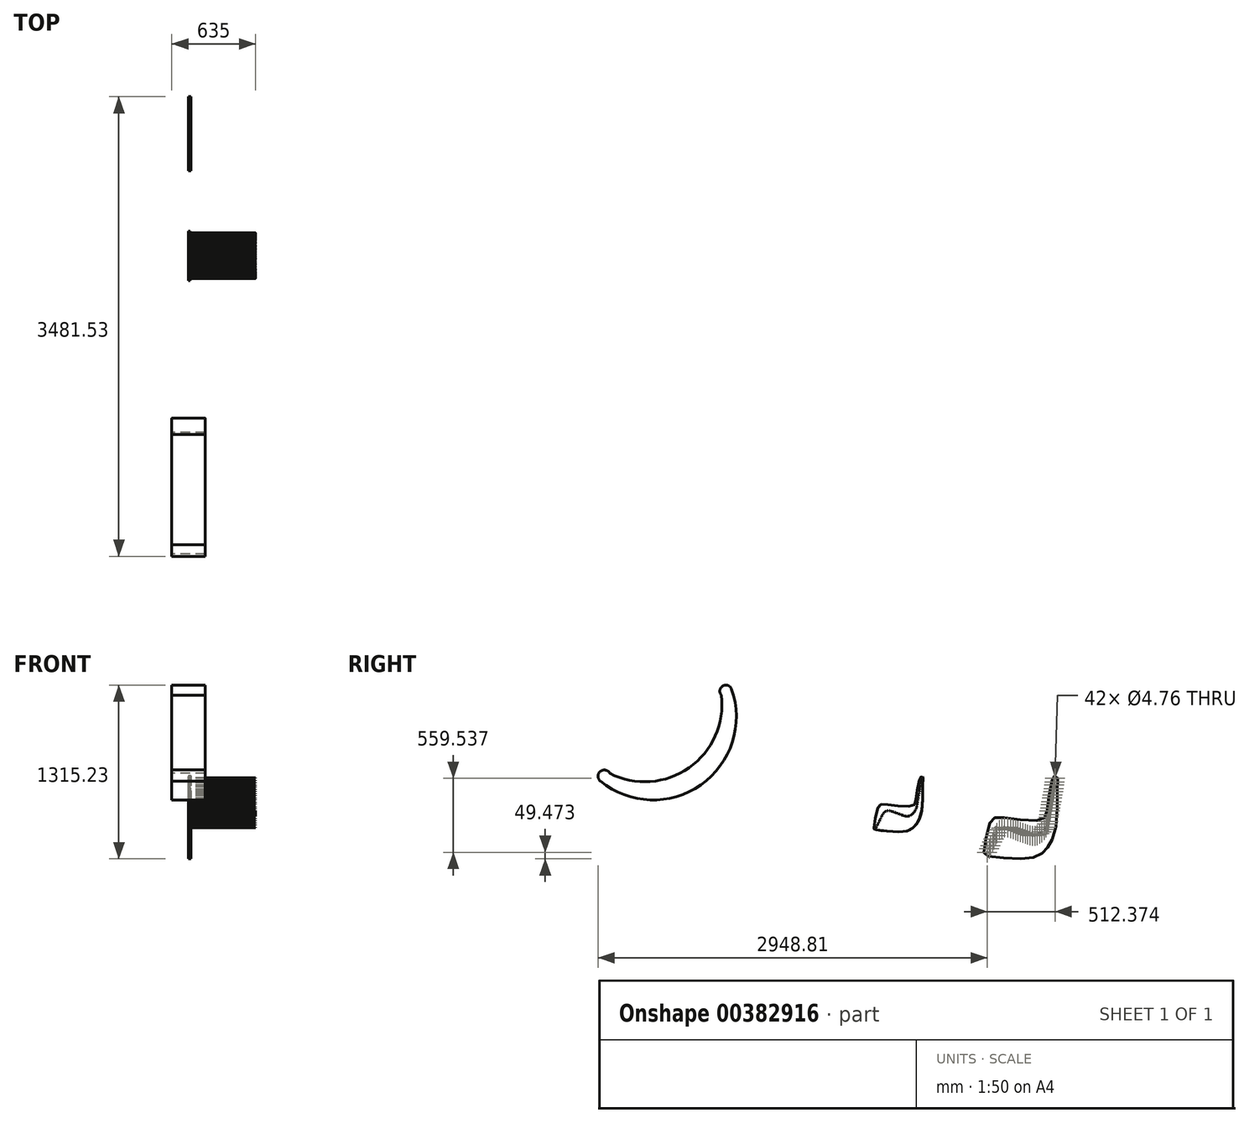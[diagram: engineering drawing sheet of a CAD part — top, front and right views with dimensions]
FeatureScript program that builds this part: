
annotation { "Feature Type Name" : "Feature", "Feature Type Description" : "" }
export const myFeature = defineFeature(function(context is Context, id is Id, definition is map)
    precondition{}
    {
        {
            var Q0;
            Q0=qCreatedBy(makeId("Right.planeOp"),FACE);
            var sketch = newSketch(context, id + "F0", { "sketchPlane" : qUnion([Q0])});
            skCircle(sketch, "E0", {"center": v(0, 0) * mm, "radius": 304.8 * mm});
            skLineSegment(sketch, "E1", {"start": v(-293.4, -82.59) * mm, "end": v(-78.09, -294.63) * mm});
            skCircle(sketch, "E2.0", {"center": v(0, 0) * mm, "radius": 381 * mm});
            skSolve(sketch);
        }
        {
            var Q0;
            Q0=qCreatedBy(makeId("Right.planeOp"),FACE);
            var sketch = newSketch(context, id + "F1", { "sketchPlane" : qUnion([Q0])});
            skArc(sketch, "E3", {"start": v(-480.61, -321.55) * mm, "mid": v(278.98, -347.7) * mm, "end": v(511.34, 375.95) * mm});
            skCircle(sketch, "E4", {"center": v(-452.9, -282.93) * mm, "radius": 47.53 * mm});
            skPoint(sketch, "E4.second.point", {"position": v(-410.62, -261.21) * mm});
            skPoint(sketch, "E4.third.point", {"position": v(-480.61, -244.32) * mm});
            skCircle(sketch, "E5", {"center": v(467.9, 361.15) * mm, "radius": 45.9 * mm});
            skPoint(sketch, "E5.second.point", {"position": v(434.1, 330.1) * mm});
            skPoint(sketch, "E5.third.point", {"position": v(424.45, 375.95) * mm});
            skArc(sketch, "E6", {"start": v(-410.62, -261.21) * mm, "mid": v(189.12, -218.95) * mm, "end": v(434.1, 330.1) * mm});
            skSolve(sketch);
        }
        {
            var Q0;
            Q0 = qSketchRegion(id + "F1", true);
            extrude(context, id + "F2", {"entities" : qUnion([Q0]), "endBound" : BoundingType.SYMMETRIC, "depth" : 254 * mm});
        }
        {
            var Q0;
            Q0=qCreatedBy(makeId("Right.planeOp"),FACE);
            var sketch = newSketch(context, id + "F3", { "sketchPlane" : qUnion([Q0])});
            skFitSpline(sketch, "E7", {"points": [v(1588.1, -672.39) * mm, v(1618.65, -522.75) * mm, v(1643, -495.6) * mm, v(1721.64, -500.28) * mm, v(1878.95, -507.77) * mm, v(1900.49, -487.17) * mm, v(1913.6, -410.39) * mm, v(1939.81, -289.6) * mm, v(1946.37, -285.85) * mm, v(1958.54, -285.79) * mm, v(1959.48, -320.5) * mm, v(1953.86, -522.75) * mm, v(1922.02, -627.62) * mm, v(1894.7, -664.12) * mm, v(1852.61, -693.43) * mm, v(1735.69, -702.53) * mm, v(1592.61, -684.79) * mm, v(1588.1, -672.39) * mm]});
            skFitSpline(sketch, "E8", {"points": [v(1839.42, 829.8) * mm, v(1806.64, 656.64) * mm, v(1782.3, 629.48) * mm, v(1703.64, 634.16) * mm, v(1546.34, 641.65) * mm, v(1524.8, 621.05) * mm, v(1511.7, 544.27) * mm, v(1485.47, 423.48) * mm, v(1478.92, 419.74) * mm, v(1466.75, 422.55) * mm, v(1465.81, 454.38) * mm, v(1471.43, 656.64) * mm, v(1503.27, 761.5) * mm, v(1546.34, 798.96) * mm, v(1596.9, 818.62) * mm, v(1689.6, 836.42) * mm, v(1834.27, 836.23) * mm, v(1839.42, 829.8) * mm]});
            skCircle(sketch, "E9", {"center": v(2585.3, 295.49) * mm, "radius": 304.8 * mm});
            skArc(sketch, "E10", {"start": v(2585.3, 295.49) * mm, "mid": v(2780.63, 386.57) * mm, "end": v(2689.55, 581.9) * mm});
            skArc(sketch, "E11", {"start": v(2585.3, 295.49) * mm, "mid": v(2389.96, 204.4) * mm, "end": v(2481.05, 9.07) * mm});
            skPoint(sketch, "E12.orphan", {"position": v(2689.55, 581.9) * mm});
            skCircle(sketch, "E13", {"center": v(2533.17, 152.28) * mm, "radius": 9.53 * mm});
            skCircle(sketch, "E14", {"center": v(2637.42, 438.7) * mm, "radius": 9.53 * mm});
            skFitSpline(sketch, "E15", {"points": [v(1606.22, -670.68) * mm, v(1621.17, -640.78) * mm, v(1637.56, -607.07) * mm, v(1653, -575.24) * mm, v(1675.01, -550.42) * mm, v(1702.63, -543.4) * mm, v(1730.26, -550.9) * mm, v(1756, -560.26) * mm, v(1780.82, -569.62) * mm, v(1805.16, -578.05) * mm, v(1829.98, -586) * mm, v(1856.2, -583.2) * mm, v(1879.14, -569.62) * mm, v(1899.74, -546.2) * mm, v(1913.31, -516.25) * mm, v(1918.93, -483.94) * mm, v(1924.55, -449.77) * mm, v(1930.64, -418.4) * mm, v(1935.63, -385.41) * mm, v(1941.76, -352) * mm, v(1945.93, -319.16) * mm, v(1949, -288.82) * mm], "startDerivative": vector(275.49, 563.46) * mm, "endDerivative": vector(62.5, 633.08) * mm});
            skCircle(sketch, "E16", {"center": v(1606.22, -670.68) * mm, "radius": 1.59 * mm});
            skCircle(sketch, "E17", {"center": v(1615.63, -651.8) * mm, "radius": 1.59 * mm});
            skCircle(sketch, "E18", {"center": v(1622.85, -637.43) * mm, "radius": 1.59 * mm});
            skCircle(sketch, "E19", {"center": v(1631.84, -619.24) * mm, "radius": 1.59 * mm});
            skCircle(sketch, "E20", {"center": v(1638.6, -604.78) * mm, "radius": 1.59 * mm});
            skCircle(sketch, "E21", {"center": v(1647.24, -586) * mm, "radius": 1.59 * mm});
            skCircle(sketch, "E22", {"center": v(1654.5, -572.78) * mm, "radius": 1.59 * mm});
            skCircle(sketch, "E23", {"center": v(1666.56, -557.28) * mm, "radius": 1.59 * mm});
            skCircle(sketch, "E24", {"center": v(1678.52, -548.4) * mm, "radius": 1.59 * mm});
            skCircle(sketch, "E25", {"center": v(1692.58, -543.84) * mm, "radius": 1.59 * mm});
            skCircle(sketch, "E26", {"center": v(1708.99, -544.23) * mm, "radius": 1.59 * mm});
            skCircle(sketch, "E27", {"center": v(1722.8, -548.17) * mm, "radius": 1.59 * mm});
            skCircle(sketch, "E28", {"center": v(1735.77, -552.9) * mm, "radius": 1.59 * mm});
            skCircle(sketch, "E29", {"center": v(1748.81, -557.6) * mm, "radius": 1.59 * mm});
            skCircle(sketch, "E30", {"center": v(1773.03, -566.76) * mm, "radius": 1.59 * mm});
            skCircle(sketch, "E31", {"center": v(1760.55, -561.98) * mm, "radius": 1.59 * mm});
            skCircle(sketch, "E32", {"center": v(1785.2, -571.14) * mm, "radius": 1.59 * mm});
            skCircle(sketch, "E33", {"center": v(1809.27, -579.63) * mm, "radius": 1.59 * mm});
            skCircle(sketch, "E34", {"center": v(1798.09, -575.5) * mm, "radius": 1.59 * mm});
            skCircle(sketch, "E35", {"center": v(1821.92, -584.19) * mm, "radius": 1.59 * mm});
            skCircle(sketch, "E36", {"center": v(1833.07, -586.35) * mm, "radius": 1.59 * mm});
            skCircle(sketch, "E37", {"center": v(1846.16, -585.75) * mm, "radius": 1.59 * mm});
            skCircle(sketch, "E38", {"center": v(1856.2, -583.2) * mm, "radius": 1.59 * mm});
            skCircle(sketch, "E39", {"center": v(1870, -576.41) * mm, "radius": 1.59 * mm});
            skCircle(sketch, "E40", {"center": v(1880.6, -568.35) * mm, "radius": 1.59 * mm});
            skCircle(sketch, "E41", {"center": v(1892.63, -555.8) * mm, "radius": 1.59 * mm});
            skCircle(sketch, "E42", {"center": v(1900.74, -544.22) * mm, "radius": 1.59 * mm});
            skCircle(sketch, "E43", {"center": v(1908.58, -528.02) * mm, "radius": 1.59 * mm});
            skCircle(sketch, "E44", {"center": v(1913.63, -514.07) * mm, "radius": 1.59 * mm});
            skCircle(sketch, "E45", {"center": v(1917.21, -494.8) * mm, "radius": 1.59 * mm});
            skCircle(sketch, "E46", {"center": v(1919.47, -480.2) * mm, "radius": 1.59 * mm});
            skCircle(sketch, "E47", {"center": v(1922.13, -461.07) * mm, "radius": 1.59 * mm});
            skCircle(sketch, "E48", {"center": v(1924.76, -447.99) * mm, "radius": 1.59 * mm});
            skCircle(sketch, "E49", {"center": v(1927.95, -429.8) * mm, "radius": 1.59 * mm});
            skCircle(sketch, "E50", {"center": v(1930.6, -415.05) * mm, "radius": 1.59 * mm});
            skCircle(sketch, "E51", {"center": v(1933.66, -396.85) * mm, "radius": 1.59 * mm});
            skCircle(sketch, "E52", {"center": v(1936.32, -381.97) * mm, "radius": 1.59 * mm});
            skCircle(sketch, "E53", {"center": v(1939.37, -364.04) * mm, "radius": 1.59 * mm});
            skCircle(sketch, "E54", {"center": v(1941.96, -349.47) * mm, "radius": 1.59 * mm});
            skCircle(sketch, "E55", {"center": v(1944.33, -330.83) * mm, "radius": 1.59 * mm});
            skCircle(sketch, "E56", {"center": v(1946.07, -316.14) * mm, "radius": 1.59 * mm});
            skCircle(sketch, "E57", {"center": v(1947.8, -297.66) * mm, "radius": 1.59 * mm});
            skLineSegment(sketch, "E58.bottom", {"start": v(2915.4, -134.35) * mm, "end": v(2331.2, -134.35) * mm});
            skLineSegment(sketch, "E58.top", {"start": v(2940.8, -743.95) * mm, "end": v(2331.2, -743.95) * mm});
            skLineSegment(sketch, "E58.left", {"start": v(2940.8, -134.35) * mm, "end": v(2940.8, -743.95) * mm});
            skLineSegment(sketch, "E58.right", {"start": v(2331.2, -134.35) * mm, "end": v(2331.2, -743.95) * mm});
            skLineSegment(sketch, "E59", {"start": v(2821.57, -439.15) * mm, "end": v(2455.55, -439.15) * mm});
            skLineSegment(sketch, "E60", {"start": v(2356.6, -743.95) * mm, "end": v(2331.2, -743.95) * mm});
            skLineSegment(sketch, "E61", {"start": v(2871.68, -396.7) * mm, "end": v(2915.4, -134.35) * mm});
            skLineSegment(sketch, "E62", {"start": v(2405.6, -480.66) * mm, "end": v(2356.6, -743.95) * mm});
            skPoint(sketch, "E63.visualSharp", {"position": v(2940.8, -134.35) * mm});
            skLineSegment(sketch, "E63.filletArc", {"start": v(2940.8, -134.35) * mm, "end": v(2940.8, -134.35) * mm});
            skPoint(sketch, "E64.visualSharp", {"position": v(2864.6, -439.15) * mm});
            skArc(sketch, "E64.filletArc", {"start": v(2821.57, -439.15) * mm, "mid": v(2854.4, -427.12) * mm, "end": v(2871.68, -396.7) * mm});
            skPoint(sketch, "E65.visualSharp", {"position": v(2413.33, -439.15) * mm});
            skArc(sketch, "E65.filletArc", {"start": v(2455.55, -439.15) * mm, "mid": v(2423.08, -450.89) * mm, "end": v(2405.6, -480.66) * mm});
            skPoint(sketch, "E66.visualSharp", {"position": v(2331.2, -134.35) * mm});
            skLineSegment(sketch, "E67.bottom", {"start": v(3735.99, -463.08) * mm, "end": v(3139.09, -463.08) * mm});
            skLineSegment(sketch, "E67.top", {"start": v(3735.99, -1072.68) * mm, "end": v(3126.39, -1072.68) * mm});
            skLineSegment(sketch, "E67.left", {"start": v(3735.99, -463.08) * mm, "end": v(3735.99, -1072.68) * mm});
            skLineSegment(sketch, "E67.right", {"start": v(3126.39, -475.78) * mm, "end": v(3126.39, -1072.68) * mm});
            skLineSegment(sketch, "E68", {"start": v(3611.45, -799.72) * mm, "end": v(3244.8, -799.72) * mm});
            skLineSegment(sketch, "E69", {"start": v(3151.79, -1072.68) * mm, "end": v(3126.39, -1072.68) * mm});
            skLineSegment(sketch, "E70", {"start": v(3661.56, -757.27) * mm, "end": v(3710.59, -463.08) * mm});
            skLineSegment(sketch, "E71", {"start": v(3194.86, -841.22) * mm, "end": v(3151.79, -1072.68) * mm});
            skPoint(sketch, "E72.visualSharp", {"position": v(3735.99, -463.08) * mm});
            skLineSegment(sketch, "E72.filletArc", {"start": v(3735.99, -463.08) * mm, "end": v(3735.99, -463.08) * mm});
            skPoint(sketch, "E73.visualSharp", {"position": v(3654.48, -799.72) * mm});
            skArc(sketch, "E73.filletArc", {"start": v(3611.45, -799.72) * mm, "mid": v(3644.28, -787.68) * mm, "end": v(3661.56, -757.27) * mm});
            skPoint(sketch, "E74.visualSharp", {"position": v(3202.59, -799.72) * mm});
            skArc(sketch, "E74.filletArc", {"start": v(3244.8, -799.72) * mm, "mid": v(3212.34, -811.45) * mm, "end": v(3194.86, -841.22) * mm});
            skPoint(sketch, "E75.visualSharp", {"position": v(3126.39, -463.08) * mm});
            skArc(sketch, "E75.filletArc", {"start": v(3139.09, -463.08) * mm, "mid": v(3130.1, -466.8) * mm, "end": v(3126.39, -475.78) * mm});
            skCircle(sketch, "E76", {"center": v(3722.26, -476.85) * mm, "radius": 13.77 * mm});
            skPoint(sketch, "E76.first.point", {"position": v(3735.99, -475.76) * mm});
            skPoint(sketch, "E76.second.point", {"position": v(3721.91, -463.08) * mm});
            skPoint(sketch, "E76.third.point", {"position": v(3708.69, -474.48) * mm});
            skLineSegment(sketch, "E77.bottom", {"start": v(3126.39, -1072.68) * mm, "end": v(3723.29, -1072.68) * mm});
            skLineSegment(sketch, "E77.top", {"start": v(3126.39, -463.08) * mm, "end": v(3735.99, -463.08) * mm});
            skLineSegment(sketch, "E77.left", {"start": v(3126.39, -1072.68) * mm, "end": v(3126.39, -463.08) * mm});
            skLineSegment(sketch, "E77.right", {"start": v(3735.99, -1059.98) * mm, "end": v(3735.99, -463.08) * mm});
            skLineSegment(sketch, "E78", {"start": v(3247.07, -759.21) * mm, "end": v(3613.26, -759.21) * mm});
            skLineSegment(sketch, "E79", {"start": v(3710.59, -463.08) * mm, "end": v(3735.99, -463.08) * mm});
            skLineSegment(sketch, "E80", {"start": v(3196.96, -801.66) * mm, "end": v(3151.79, -1072.68) * mm});
            skLineSegment(sketch, "E81", {"start": v(3663.2, -717.7) * mm, "end": v(3710.59, -463.08) * mm});
            skPoint(sketch, "E82.visualSharp", {"position": v(3126.39, -1072.68) * mm});
            skLineSegment(sketch, "E82.filletArc", {"start": v(4374.58, -603.6) * mm, "end": v(4374.58, -603.6) * mm});
            skPoint(sketch, "E83.visualSharp", {"position": v(3204.03, -759.21) * mm});
            skArc(sketch, "E83.filletArc", {"start": v(3247.07, -759.21) * mm, "mid": v(3214.23, -771.25) * mm, "end": v(3196.96, -801.66) * mm});
            skPoint(sketch, "E84.visualSharp", {"position": v(3655.47, -759.21) * mm});
            skArc(sketch, "E84.filletArc", {"start": v(3613.26, -759.21) * mm, "mid": v(3645.73, -747.48) * mm, "end": v(3663.2, -717.7) * mm});
            skPoint(sketch, "E85.visualSharp", {"position": v(3735.99, -1072.68) * mm});
            skArc(sketch, "E85.filletArc", {"start": v(3723.29, -1072.68) * mm, "mid": v(3732.27, -1068.96) * mm, "end": v(3735.99, -1059.98) * mm});
            skCircle(sketch, "E86", {"center": v(3140.12, -1058.91) * mm, "radius": 13.77 * mm});
            skPoint(sketch, "E86.first.point", {"position": v(3126.39, -1060) * mm});
            skPoint(sketch, "E86.second.point", {"position": v(3140.46, -1072.68) * mm});
            skPoint(sketch, "E86.third.point", {"position": v(3153.69, -1061.28) * mm});
            skFitSpline(sketch, "E87", {"points": [v(3126.39, -802.07) * mm, v(3137.63, -603.35) * mm, v(3162.08, -502.39) * mm, v(3219.46, -474.76) * mm, v(3365.05, -463.08) * mm, v(3593.52, -474.76) * mm, v(3690.22, -491.76) * mm, v(3700.6, -516.75) * mm], "startDerivative": vector(49.41, 1106.55) * mm, "endDerivative": vector(-78.89, -413.64) * mm});
            skLineSegment(sketch, "E88", {"start": v(2940.8, -134.35) * mm, "end": v(2915.4, -134.35) * mm});
            skFitSpline(sketch, "E89", {"points": [v(2331.2, -478.04) * mm, v(2342.68, -279.5) * mm, v(2367.12, -178.54) * mm, v(2424.5, -150.9) * mm, v(2570.1, -139.23) * mm, v(2798.57, -150.9) * mm, v(2895.27, -167.91) * mm, v(2905.65, -192.9) * mm], "startDerivative": vector(49.41, 1106.55) * mm, "endDerivative": vector(-68.57, -411.43) * mm});
            skCircle(sketch, "E90", {"center": v(2999.57, -107.75) * mm, "radius": 19.05 * mm});
            skFitSpline(sketch, "E91", {"points": [v(3299.06, -138.7) * mm, v(3304.9, -135.23) * mm, v(3310.44, -129.86) * mm, v(3312.49, -123.07) * mm, v(3309.8, -115.49) * mm, v(3304.12, -110.59) * mm, v(3297.32, -107.59) * mm, v(3290.37, -105.53) * mm, v(3283.9, -104.43) * mm, v(3276.63, -105.85) * mm, v(3269.84, -109.33) * mm, v(3266.68, -113.75) * mm, v(3268.42, -114.54) * mm, v(3272.05, -113.75) * mm, v(3278.37, -112.49) * mm, v(3281.69, -112.17) * mm, v(3283.27, -112.49) * mm, v(3279.63, -112.8) * mm, v(3273, -114.7) * mm, v(3266.52, -117.38) * mm, v(3260.83, -122.28) * mm, v(3256.41, -127.5) * mm, v(3253.1, -135.08) * mm, v(3256.25, -131.6) * mm, v(3257.1, -132.53) * mm, v(3259.1, -133.37) * mm, v(3262.68, -133.03) * mm, v(3269.29, -130.48) * mm, v(3277.66, -127.4) * mm, v(3287.77, -125.03) * mm, v(3295.35, -123.84) * mm, v(3300.8, -124.32) * mm, v(3303.01, -126.53) * mm, v(3303.64, -130.87) * mm, v(3302.07, -135.22) * mm, v(3298.8, -138.98) * mm, v(3298.8, -139) * mm], "startDerivative": vector(185.96, 100.47) * mm, "endDerivative": vector(3.82, -6.21) * mm});
            skFitSpline(sketch, "E92", {"points": [v(3287, -104.73) * mm, v(3284.28, -101.52) * mm, v(3275.78, -96.34) * mm, v(3258.25, -92.09) * mm, v(3234.87, -91.82) * mm, v(3213.88, -94.35) * mm, v(3191.56, -100.99) * mm, v(3174.7, -110.42) * mm, v(3167.26, -116.27) * mm], "startDerivative": vector(-33.94, 48.22) * mm, "endDerivative": vector(-67.07, -56.56) * mm});
            skFitSpline(sketch, "E93", {"points": [v(3167.26, -116.27) * mm, v(3178.56, -117.97) * mm, v(3187.4, -121.35) * mm], "startDerivative": vector(22.38, -2.25) * mm, "endDerivative": vector(17.81, -8.02) * mm});
            skLineSegment(sketch, "E94", {"start": v(3313.38, 1676.84) * mm, "end": v(3431.71, 1235.22) * mm});
            skLineSegment(sketch, "E95", {"start": v(3431.71, 1235.22) * mm, "end": v(3873.33, 1353.55) * mm});
            skLineSegment(sketch, "E96", {"start": v(3873.33, 1353.55) * mm, "end": v(3873.33, 1251.95) * mm});
            skLineSegment(sketch, "E97", {"start": v(3873.33, 1251.95) * mm, "end": v(3771.73, 1251.95) * mm});
            skLineSegment(sketch, "E98", {"start": v(3771.73, 1251.95) * mm, "end": v(3771.73, 1150.35) * mm});
            skLineSegment(sketch, "E99", {"start": v(3771.73, 1150.35) * mm, "end": v(3251.9, 1150.35) * mm});
            skLineSegment(sketch, "E100", {"start": v(3251.9, 1150.35) * mm, "end": v(3251.9, 1724.42) * mm});
            skLineSegment(sketch, "E101", {"start": v(3735.99, -761.53) * mm, "end": v(2999.92, -767.88) * mm, "construction": true});
            skPoint(sketch, "E101.endSnap0", {"position": v(3735.99, -767.88) * mm});
            skSolve(sketch);
        }
        {
            var Q0;
            Q0=makeQuery(id+"F3.imprint","IMPRINT",FACE,{"disambiguationData":[TD([[makeQuery(id+"F3.imprint","IMPRINT",EDGE,{"derivedFrom":sQuery(id+"F3.wireOp",EDGE,"E7")}),-1.0]])]});
            extrude(context, id + "F4", {"entities" : qUnion([Q0]), "depth" : 12.7 * mm});
        }
        {
            var Q0;
            Q0=makeQuery(id+"F4.opExtrude","SWEPT_BODY",BODY,{"disambiguationData":[OSD([sQuery(id+"F3.wireOp",EDGE,"E7")])]});
            var Q1;
            Q1=sQuery(id+"F0.wireOp",VERTEX,"E1.end");
            transform(context, id + "F5", {"entities" : qUnion([Q0]), "transformType" : TransformType.SCALE_UNIFORMLY, "scale" : 1.5, "scalePoint" : qUnion([Q1]), "makeCopy" : true});
        }
        {
            var Q0;
            {var subQ0=sQuery(id+"F3.wireOp",EDGE,"E35");var subQ1=sQuery(id+"F3.wireOp",EDGE,"E15");var subQ2=makeQuery(id+"F3.imprint","INTERSECT",VERTEX,{"disambiguationData":[OD(0.0)],"derivedFrom":[subQ1,subQ0]});Q0=makeQuery(id+"F3.imprint","IMPRINT",FACE,{"disambiguationData":[TD([[makeQuery(id+"F3.imprint","IMPRINT",EDGE,{"disambiguationData":[TD([[subQ2,-1.0]])],"derivedFrom":subQ1}),-1.0]])]});}
            var Q1;
            {var subQ0=sQuery(id+"F3.wireOp",EDGE,"E27");var subQ1=sQuery(id+"F3.wireOp",EDGE,"E15");var subQ2=makeQuery(id+"F3.imprint","INTERSECT",VERTEX,{"disambiguationData":[OD(0.0)],"derivedFrom":[subQ1,subQ0]});Q1=makeQuery(id+"F3.imprint","IMPRINT",FACE,{"disambiguationData":[TD([[makeQuery(id+"F3.imprint","IMPRINT",EDGE,{"disambiguationData":[TD([[subQ2,-1.0]])],"derivedFrom":subQ1}),-1.0]])]});}
            var Q2;
            {var subQ0=sQuery(id+"F3.wireOp",EDGE,"E39");var subQ1=sQuery(id+"F3.wireOp",EDGE,"E15");var subQ2=makeQuery(id+"F3.imprint","INTERSECT",VERTEX,{"disambiguationData":[OD(0.0)],"derivedFrom":[subQ1,subQ0]});Q2=makeQuery(id+"F3.imprint","IMPRINT",FACE,{"disambiguationData":[TD([[makeQuery(id+"F3.imprint","IMPRINT",EDGE,{"disambiguationData":[TD([[subQ2,-1.0]])],"derivedFrom":subQ1}),1.0]])]});}
            var Q3;
            {var subQ0=sQuery(id+"F3.wireOp",EDGE,"E32");var subQ1=sQuery(id+"F3.wireOp",EDGE,"E15");var subQ2=makeQuery(id+"F3.imprint","INTERSECT",VERTEX,{"disambiguationData":[OD(0.0)],"derivedFrom":[subQ1,subQ0]});Q3=makeQuery(id+"F3.imprint","IMPRINT",FACE,{"disambiguationData":[TD([[makeQuery(id+"F3.imprint","IMPRINT",EDGE,{"disambiguationData":[TD([[subQ2,-1.0]])],"derivedFrom":subQ1}),-1.0]])]});}
            var Q4;
            {var subQ0=sQuery(id+"F3.wireOp",EDGE,"E24");var subQ1=sQuery(id+"F3.wireOp",EDGE,"E15");var subQ2=makeQuery(id+"F3.imprint","INTERSECT",VERTEX,{"disambiguationData":[OD(0.0)],"derivedFrom":[subQ1,subQ0]});Q4=makeQuery(id+"F3.imprint","IMPRINT",FACE,{"disambiguationData":[TD([[makeQuery(id+"F3.imprint","IMPRINT",EDGE,{"disambiguationData":[TD([[subQ2,-1.0]])],"derivedFrom":subQ1}),1.0]])]});}
            var Q5;
            {var subQ0=sQuery(id+"F3.wireOp",EDGE,"E29");var subQ1=sQuery(id+"F3.wireOp",EDGE,"E15");var subQ2=makeQuery(id+"F3.imprint","INTERSECT",VERTEX,{"disambiguationData":[OD(0.0)],"derivedFrom":[subQ1,subQ0]});Q5=makeQuery(id+"F3.imprint","IMPRINT",FACE,{"disambiguationData":[TD([[makeQuery(id+"F3.imprint","IMPRINT",EDGE,{"disambiguationData":[TD([[subQ2,-1.0]])],"derivedFrom":subQ1}),-1.0]])]});}
            var Q6;
            {var subQ0=sQuery(id+"F3.wireOp",EDGE,"E42");var subQ1=sQuery(id+"F3.wireOp",EDGE,"E15");var subQ2=makeQuery(id+"F3.imprint","INTERSECT",VERTEX,{"disambiguationData":[OD(0.0)],"derivedFrom":[subQ1,subQ0]});Q6=makeQuery(id+"F3.imprint","IMPRINT",FACE,{"disambiguationData":[TD([[makeQuery(id+"F3.imprint","IMPRINT",EDGE,{"disambiguationData":[TD([[subQ2,-1.0]])],"derivedFrom":subQ1}),1.0]])]});}
            var Q7;
            {var subQ0=sQuery(id+"F3.wireOp",EDGE,"E33");var subQ1=sQuery(id+"F3.wireOp",EDGE,"E15");var subQ2=makeQuery(id+"F3.imprint","INTERSECT",VERTEX,{"disambiguationData":[OD(0.0)],"derivedFrom":[subQ1,subQ0]});Q7=makeQuery(id+"F3.imprint","IMPRINT",FACE,{"disambiguationData":[TD([[makeQuery(id+"F3.imprint","IMPRINT",EDGE,{"disambiguationData":[TD([[subQ2,-1.0]])],"derivedFrom":subQ1}),-1.0]])]});}
            var Q8;
            {var subQ0=sQuery(id+"F3.wireOp",EDGE,"E27");var subQ1=sQuery(id+"F3.wireOp",EDGE,"E15");var subQ2=makeQuery(id+"F3.imprint","INTERSECT",VERTEX,{"disambiguationData":[OD(0.0)],"derivedFrom":[subQ1,subQ0]});Q8=makeQuery(id+"F3.imprint","IMPRINT",FACE,{"disambiguationData":[TD([[makeQuery(id+"F3.imprint","IMPRINT",EDGE,{"disambiguationData":[TD([[subQ2,-1.0]])],"derivedFrom":subQ1}),1.0]])]});}
            var Q9;
            {var subQ0=sQuery(id+"F3.wireOp",EDGE,"E29");var subQ1=sQuery(id+"F3.wireOp",EDGE,"E15");var subQ2=makeQuery(id+"F3.imprint","INTERSECT",VERTEX,{"disambiguationData":[OD(0.0)],"derivedFrom":[subQ1,subQ0]});Q9=makeQuery(id+"F3.imprint","IMPRINT",FACE,{"disambiguationData":[TD([[makeQuery(id+"F3.imprint","IMPRINT",EDGE,{"disambiguationData":[TD([[subQ2,-1.0]])],"derivedFrom":subQ1}),1.0]])]});}
            var Q10;
            {var subQ0=sQuery(id+"F3.wireOp",EDGE,"E25");var subQ1=sQuery(id+"F3.wireOp",EDGE,"E15");var subQ2=makeQuery(id+"F3.imprint","INTERSECT",VERTEX,{"disambiguationData":[OD(0.0)],"derivedFrom":[subQ1,subQ0]});Q10=makeQuery(id+"F3.imprint","IMPRINT",FACE,{"disambiguationData":[TD([[makeQuery(id+"F3.imprint","IMPRINT",EDGE,{"disambiguationData":[TD([[subQ2,-1.0]])],"derivedFrom":subQ1}),1.0]])]});}
            var Q11;
            {var subQ0=sQuery(id+"F3.wireOp",EDGE,"E23");var subQ1=sQuery(id+"F3.wireOp",EDGE,"E15");var subQ2=makeQuery(id+"F3.imprint","INTERSECT",VERTEX,{"disambiguationData":[OD(0.0)],"derivedFrom":[subQ1,subQ0]});Q11=makeQuery(id+"F3.imprint","IMPRINT",FACE,{"disambiguationData":[TD([[makeQuery(id+"F3.imprint","IMPRINT",EDGE,{"disambiguationData":[TD([[subQ2,-1.0]])],"derivedFrom":subQ1}),1.0]])]});}
            var Q12;
            {var subQ0=sQuery(id+"F3.wireOp",EDGE,"E36");var subQ1=sQuery(id+"F3.wireOp",EDGE,"E15");var subQ2=makeQuery(id+"F3.imprint","INTERSECT",VERTEX,{"disambiguationData":[OD(0.0)],"derivedFrom":[subQ1,subQ0]});Q12=makeQuery(id+"F3.imprint","IMPRINT",FACE,{"disambiguationData":[TD([[makeQuery(id+"F3.imprint","IMPRINT",EDGE,{"disambiguationData":[TD([[subQ2,-1.0]])],"derivedFrom":subQ1}),1.0]])]});}
            var Q13;
            {var subQ0=sQuery(id+"F3.wireOp",EDGE,"E21");var subQ1=sQuery(id+"F3.wireOp",EDGE,"E15");var subQ2=makeQuery(id+"F3.imprint","INTERSECT",VERTEX,{"disambiguationData":[OD(0.0)],"derivedFrom":[subQ1,subQ0]});Q13=makeQuery(id+"F3.imprint","IMPRINT",FACE,{"disambiguationData":[TD([[makeQuery(id+"F3.imprint","IMPRINT",EDGE,{"disambiguationData":[TD([[subQ2,-1.0]])],"derivedFrom":subQ1}),1.0]])]});}
            var Q14;
            {var subQ0=sQuery(id+"F3.wireOp",EDGE,"E30");var subQ1=sQuery(id+"F3.wireOp",EDGE,"E15");var subQ2=makeQuery(id+"F3.imprint","INTERSECT",VERTEX,{"disambiguationData":[OD(0.0)],"derivedFrom":[subQ1,subQ0]});Q14=makeQuery(id+"F3.imprint","IMPRINT",FACE,{"disambiguationData":[TD([[makeQuery(id+"F3.imprint","IMPRINT",EDGE,{"disambiguationData":[TD([[subQ2,-1.0]])],"derivedFrom":subQ1}),-1.0]])]});}
            var Q15;
            {var subQ0=sQuery(id+"F3.wireOp",EDGE,"E33");var subQ1=sQuery(id+"F3.wireOp",EDGE,"E15");var subQ2=makeQuery(id+"F3.imprint","INTERSECT",VERTEX,{"disambiguationData":[OD(0.0)],"derivedFrom":[subQ1,subQ0]});Q15=makeQuery(id+"F3.imprint","IMPRINT",FACE,{"disambiguationData":[TD([[makeQuery(id+"F3.imprint","IMPRINT",EDGE,{"disambiguationData":[TD([[subQ2,-1.0]])],"derivedFrom":subQ1}),1.0]])]});}
            var Q16;
            {var subQ0=sQuery(id+"F3.wireOp",EDGE,"E31");var subQ1=sQuery(id+"F3.wireOp",EDGE,"E15");var subQ2=makeQuery(id+"F3.imprint","INTERSECT",VERTEX,{"disambiguationData":[OD(0.0)],"derivedFrom":[subQ1,subQ0]});Q16=makeQuery(id+"F3.imprint","IMPRINT",FACE,{"disambiguationData":[TD([[makeQuery(id+"F3.imprint","IMPRINT",EDGE,{"disambiguationData":[TD([[subQ2,-1.0]])],"derivedFrom":subQ1}),1.0]])]});}
            var Q17;
            {var subQ0=sQuery(id+"F3.wireOp",EDGE,"E23");var subQ1=sQuery(id+"F3.wireOp",EDGE,"E15");var subQ2=makeQuery(id+"F3.imprint","INTERSECT",VERTEX,{"disambiguationData":[OD(0.0)],"derivedFrom":[subQ1,subQ0]});Q17=makeQuery(id+"F3.imprint","IMPRINT",FACE,{"disambiguationData":[TD([[makeQuery(id+"F3.imprint","IMPRINT",EDGE,{"disambiguationData":[TD([[subQ2,-1.0]])],"derivedFrom":subQ1}),-1.0]])]});}
            var Q18;
            {var subQ0=sQuery(id+"F3.wireOp",EDGE,"E28");var subQ1=sQuery(id+"F3.wireOp",EDGE,"E15");var subQ2=makeQuery(id+"F3.imprint","INTERSECT",VERTEX,{"disambiguationData":[OD(0.0)],"derivedFrom":[subQ1,subQ0]});Q18=makeQuery(id+"F3.imprint","IMPRINT",FACE,{"disambiguationData":[TD([[makeQuery(id+"F3.imprint","IMPRINT",EDGE,{"disambiguationData":[TD([[subQ2,-1.0]])],"derivedFrom":subQ1}),-1.0]])]});}
            var Q19;
            {var subQ0=sQuery(id+"F3.wireOp",EDGE,"E26");var subQ1=sQuery(id+"F3.wireOp",EDGE,"E15");var subQ2=makeQuery(id+"F3.imprint","INTERSECT",VERTEX,{"disambiguationData":[OD(0.0)],"derivedFrom":[subQ1,subQ0]});Q19=makeQuery(id+"F3.imprint","IMPRINT",FACE,{"disambiguationData":[TD([[makeQuery(id+"F3.imprint","IMPRINT",EDGE,{"disambiguationData":[TD([[subQ2,-1.0]])],"derivedFrom":subQ1}),1.0]])]});}
            var Q20;
            {var subQ0=sQuery(id+"F3.wireOp",EDGE,"E36");var subQ1=sQuery(id+"F3.wireOp",EDGE,"E15");var subQ2=makeQuery(id+"F3.imprint","INTERSECT",VERTEX,{"disambiguationData":[OD(0.0)],"derivedFrom":[subQ1,subQ0]});Q20=makeQuery(id+"F3.imprint","IMPRINT",FACE,{"disambiguationData":[TD([[makeQuery(id+"F3.imprint","IMPRINT",EDGE,{"disambiguationData":[TD([[subQ2,-1.0]])],"derivedFrom":subQ1}),-1.0]])]});}
            var Q21;
            {var subQ0=sQuery(id+"F3.wireOp",EDGE,"E37");var subQ1=sQuery(id+"F3.wireOp",EDGE,"E15");var subQ2=makeQuery(id+"F3.imprint","INTERSECT",VERTEX,{"disambiguationData":[OD(0.0)],"derivedFrom":[subQ1,subQ0]});Q21=makeQuery(id+"F3.imprint","IMPRINT",FACE,{"disambiguationData":[TD([[makeQuery(id+"F3.imprint","IMPRINT",EDGE,{"disambiguationData":[TD([[subQ2,-1.0]])],"derivedFrom":subQ1}),1.0]])]});}
            var Q22;
            {var subQ0=sQuery(id+"F3.wireOp",EDGE,"E41");var subQ1=sQuery(id+"F3.wireOp",EDGE,"E15");var subQ2=makeQuery(id+"F3.imprint","INTERSECT",VERTEX,{"disambiguationData":[OD(0.0)],"derivedFrom":[subQ1,subQ0]});Q22=makeQuery(id+"F3.imprint","IMPRINT",FACE,{"disambiguationData":[TD([[makeQuery(id+"F3.imprint","IMPRINT",EDGE,{"disambiguationData":[TD([[subQ2,-1.0]])],"derivedFrom":subQ1}),-1.0]])]});}
            var Q23;
            {var subQ0=sQuery(id+"F3.wireOp",EDGE,"E34");var subQ1=sQuery(id+"F3.wireOp",EDGE,"E15");var subQ2=makeQuery(id+"F3.imprint","INTERSECT",VERTEX,{"disambiguationData":[OD(0.0)],"derivedFrom":[subQ1,subQ0]});Q23=makeQuery(id+"F3.imprint","IMPRINT",FACE,{"disambiguationData":[TD([[makeQuery(id+"F3.imprint","IMPRINT",EDGE,{"disambiguationData":[TD([[subQ2,-1.0]])],"derivedFrom":subQ1}),1.0]])]});}
            var Q24;
            {var subQ0=sQuery(id+"F3.wireOp",EDGE,"E37");var subQ1=sQuery(id+"F3.wireOp",EDGE,"E15");var subQ2=makeQuery(id+"F3.imprint","INTERSECT",VERTEX,{"disambiguationData":[OD(0.0)],"derivedFrom":[subQ1,subQ0]});Q24=makeQuery(id+"F3.imprint","IMPRINT",FACE,{"disambiguationData":[TD([[makeQuery(id+"F3.imprint","IMPRINT",EDGE,{"disambiguationData":[TD([[subQ2,-1.0]])],"derivedFrom":subQ1}),-1.0]])]});}
            var Q25;
            {var subQ0=sQuery(id+"F3.wireOp",EDGE,"E30");var subQ1=sQuery(id+"F3.wireOp",EDGE,"E15");var subQ2=makeQuery(id+"F3.imprint","INTERSECT",VERTEX,{"disambiguationData":[OD(0.0)],"derivedFrom":[subQ1,subQ0]});Q25=makeQuery(id+"F3.imprint","IMPRINT",FACE,{"disambiguationData":[TD([[makeQuery(id+"F3.imprint","IMPRINT",EDGE,{"disambiguationData":[TD([[subQ2,-1.0]])],"derivedFrom":subQ1}),1.0]])]});}
            var Q26;
            {var subQ0=sQuery(id+"F3.wireOp",EDGE,"E40");var subQ1=sQuery(id+"F3.wireOp",EDGE,"E15");var subQ2=makeQuery(id+"F3.imprint","INTERSECT",VERTEX,{"disambiguationData":[OD(0.0)],"derivedFrom":[subQ1,subQ0]});Q26=makeQuery(id+"F3.imprint","IMPRINT",FACE,{"disambiguationData":[TD([[makeQuery(id+"F3.imprint","IMPRINT",EDGE,{"disambiguationData":[TD([[subQ2,-1.0]])],"derivedFrom":subQ1}),1.0]])]});}
            var Q27;
            {var subQ0=sQuery(id+"F3.wireOp",EDGE,"E21");var subQ1=sQuery(id+"F3.wireOp",EDGE,"E15");var subQ2=makeQuery(id+"F3.imprint","INTERSECT",VERTEX,{"disambiguationData":[OD(0.0)],"derivedFrom":[subQ1,subQ0]});Q27=makeQuery(id+"F3.imprint","IMPRINT",FACE,{"disambiguationData":[TD([[makeQuery(id+"F3.imprint","IMPRINT",EDGE,{"disambiguationData":[TD([[subQ2,-1.0]])],"derivedFrom":subQ1}),-1.0]])]});}
            var Q28;
            {var subQ0=sQuery(id+"F3.wireOp",EDGE,"E34");var subQ1=sQuery(id+"F3.wireOp",EDGE,"E15");var subQ2=makeQuery(id+"F3.imprint","INTERSECT",VERTEX,{"disambiguationData":[OD(0.0)],"derivedFrom":[subQ1,subQ0]});Q28=makeQuery(id+"F3.imprint","IMPRINT",FACE,{"disambiguationData":[TD([[makeQuery(id+"F3.imprint","IMPRINT",EDGE,{"disambiguationData":[TD([[subQ2,-1.0]])],"derivedFrom":subQ1}),-1.0]])]});}
            var Q29;
            {var subQ0=sQuery(id+"F3.wireOp",EDGE,"E26");var subQ1=sQuery(id+"F3.wireOp",EDGE,"E15");var subQ2=makeQuery(id+"F3.imprint","INTERSECT",VERTEX,{"disambiguationData":[OD(0.0)],"derivedFrom":[subQ1,subQ0]});Q29=makeQuery(id+"F3.imprint","IMPRINT",FACE,{"disambiguationData":[TD([[makeQuery(id+"F3.imprint","IMPRINT",EDGE,{"disambiguationData":[TD([[subQ2,-1.0]])],"derivedFrom":subQ1}),-1.0]])]});}
            var Q30;
            {var subQ0=sQuery(id+"F3.wireOp",EDGE,"E31");var subQ1=sQuery(id+"F3.wireOp",EDGE,"E15");var subQ2=makeQuery(id+"F3.imprint","INTERSECT",VERTEX,{"disambiguationData":[OD(0.0)],"derivedFrom":[subQ1,subQ0]});Q30=makeQuery(id+"F3.imprint","IMPRINT",FACE,{"disambiguationData":[TD([[makeQuery(id+"F3.imprint","IMPRINT",EDGE,{"disambiguationData":[TD([[subQ2,-1.0]])],"derivedFrom":subQ1}),-1.0]])]});}
            var Q31;
            {var subQ0=sQuery(id+"F3.wireOp",EDGE,"E22");var subQ1=sQuery(id+"F3.wireOp",EDGE,"E15");var subQ2=makeQuery(id+"F3.imprint","INTERSECT",VERTEX,{"disambiguationData":[OD(0.0)],"derivedFrom":[subQ1,subQ0]});Q31=makeQuery(id+"F3.imprint","IMPRINT",FACE,{"disambiguationData":[TD([[makeQuery(id+"F3.imprint","IMPRINT",EDGE,{"disambiguationData":[TD([[subQ2,-1.0]])],"derivedFrom":subQ1}),1.0]])]});}
            var Q32;
            {var subQ0=sQuery(id+"F3.wireOp",EDGE,"E25");var subQ1=sQuery(id+"F3.wireOp",EDGE,"E15");var subQ2=makeQuery(id+"F3.imprint","INTERSECT",VERTEX,{"disambiguationData":[OD(0.0)],"derivedFrom":[subQ1,subQ0]});Q32=makeQuery(id+"F3.imprint","IMPRINT",FACE,{"disambiguationData":[TD([[makeQuery(id+"F3.imprint","IMPRINT",EDGE,{"disambiguationData":[TD([[subQ2,-1.0]])],"derivedFrom":subQ1}),-1.0]])]});}
            var Q33;
            {var subQ0=sQuery(id+"F3.wireOp",EDGE,"E28");var subQ1=sQuery(id+"F3.wireOp",EDGE,"E15");var subQ2=makeQuery(id+"F3.imprint","INTERSECT",VERTEX,{"disambiguationData":[OD(0.0)],"derivedFrom":[subQ1,subQ0]});Q33=makeQuery(id+"F3.imprint","IMPRINT",FACE,{"disambiguationData":[TD([[makeQuery(id+"F3.imprint","IMPRINT",EDGE,{"disambiguationData":[TD([[subQ2,-1.0]])],"derivedFrom":subQ1}),1.0]])]});}
            var Q34;
            {var subQ0=sQuery(id+"F3.wireOp",EDGE,"E35");var subQ1=sQuery(id+"F3.wireOp",EDGE,"E15");var subQ2=makeQuery(id+"F3.imprint","INTERSECT",VERTEX,{"disambiguationData":[OD(0.0)],"derivedFrom":[subQ1,subQ0]});Q34=makeQuery(id+"F3.imprint","IMPRINT",FACE,{"disambiguationData":[TD([[makeQuery(id+"F3.imprint","IMPRINT",EDGE,{"disambiguationData":[TD([[subQ2,-1.0]])],"derivedFrom":subQ1}),1.0]])]});}
            var Q35;
            {var subQ0=sQuery(id+"F3.wireOp",EDGE,"E24");var subQ1=sQuery(id+"F3.wireOp",EDGE,"E15");var subQ2=makeQuery(id+"F3.imprint","INTERSECT",VERTEX,{"disambiguationData":[OD(0.0)],"derivedFrom":[subQ1,subQ0]});Q35=makeQuery(id+"F3.imprint","IMPRINT",FACE,{"disambiguationData":[TD([[makeQuery(id+"F3.imprint","IMPRINT",EDGE,{"disambiguationData":[TD([[subQ2,-1.0]])],"derivedFrom":subQ1}),-1.0]])]});}
            var Q36;
            {var subQ0=sQuery(id+"F3.wireOp",EDGE,"E41");var subQ1=sQuery(id+"F3.wireOp",EDGE,"E15");var subQ2=makeQuery(id+"F3.imprint","INTERSECT",VERTEX,{"disambiguationData":[OD(0.0)],"derivedFrom":[subQ1,subQ0]});Q36=makeQuery(id+"F3.imprint","IMPRINT",FACE,{"disambiguationData":[TD([[makeQuery(id+"F3.imprint","IMPRINT",EDGE,{"disambiguationData":[TD([[subQ2,-1.0]])],"derivedFrom":subQ1}),1.0]])]});}
            var Q37;
            {var subQ0=sQuery(id+"F3.wireOp",EDGE,"E42");var subQ1=sQuery(id+"F3.wireOp",EDGE,"E15");var subQ2=makeQuery(id+"F3.imprint","INTERSECT",VERTEX,{"disambiguationData":[OD(0.0)],"derivedFrom":[subQ1,subQ0]});Q37=makeQuery(id+"F3.imprint","IMPRINT",FACE,{"disambiguationData":[TD([[makeQuery(id+"F3.imprint","IMPRINT",EDGE,{"disambiguationData":[TD([[subQ2,-1.0]])],"derivedFrom":subQ1}),-1.0]])]});}
            var Q38;
            {var subQ0=sQuery(id+"F3.wireOp",EDGE,"E40");var subQ1=sQuery(id+"F3.wireOp",EDGE,"E15");var subQ2=makeQuery(id+"F3.imprint","INTERSECT",VERTEX,{"disambiguationData":[OD(0.0)],"derivedFrom":[subQ1,subQ0]});Q38=makeQuery(id+"F3.imprint","IMPRINT",FACE,{"disambiguationData":[TD([[makeQuery(id+"F3.imprint","IMPRINT",EDGE,{"disambiguationData":[TD([[subQ2,-1.0]])],"derivedFrom":subQ1}),-1.0]])]});}
            var Q39;
            {var subQ0=sQuery(id+"F3.wireOp",EDGE,"9f402305-efcd-4aa8-bc8a-3394f6d3dfb0");var subQ1=sQuery(id+"F3.wireOp",EDGE,"E15");var subQ2=makeQuery(id+"F3.imprint","INTERSECT",VERTEX,{"disambiguationData":[OD(0.0)],"derivedFrom":[subQ1,subQ0]});Q39=makeQuery(id+"F3.imprint","IMPRINT",FACE,{"disambiguationData":[TD([[makeQuery(id+"F3.imprint","IMPRINT",EDGE,{"disambiguationData":[TD([[subQ2,-1.0]])],"derivedFrom":subQ1}),1.0]])]});}
            var Q40;
            {var subQ0=sQuery(id+"F3.wireOp",EDGE,"E39");var subQ1=sQuery(id+"F3.wireOp",EDGE,"E15");var subQ2=makeQuery(id+"F3.imprint","INTERSECT",VERTEX,{"disambiguationData":[OD(0.0)],"derivedFrom":[subQ1,subQ0]});Q40=makeQuery(id+"F3.imprint","IMPRINT",FACE,{"disambiguationData":[TD([[makeQuery(id+"F3.imprint","IMPRINT",EDGE,{"disambiguationData":[TD([[subQ2,-1.0]])],"derivedFrom":subQ1}),-1.0]])]});}
            var Q41;
            {var subQ0=sQuery(id+"F3.wireOp",EDGE,"E22");var subQ1=sQuery(id+"F3.wireOp",EDGE,"E15");var subQ2=makeQuery(id+"F3.imprint","INTERSECT",VERTEX,{"disambiguationData":[OD(0.0)],"derivedFrom":[subQ1,subQ0]});Q41=makeQuery(id+"F3.imprint","IMPRINT",FACE,{"disambiguationData":[TD([[makeQuery(id+"F3.imprint","IMPRINT",EDGE,{"disambiguationData":[TD([[subQ2,-1.0]])],"derivedFrom":subQ1}),-1.0]])]});}
            var Q42;
            {var subQ0=sQuery(id+"F3.wireOp",EDGE,"E32");var subQ1=sQuery(id+"F3.wireOp",EDGE,"E15");var subQ2=makeQuery(id+"F3.imprint","INTERSECT",VERTEX,{"disambiguationData":[OD(0.0)],"derivedFrom":[subQ1,subQ0]});Q42=makeQuery(id+"F3.imprint","IMPRINT",FACE,{"disambiguationData":[TD([[makeQuery(id+"F3.imprint","IMPRINT",EDGE,{"disambiguationData":[TD([[subQ2,-1.0]])],"derivedFrom":subQ1}),1.0]])]});}
            var Q43;
            {var subQ0=sQuery(id+"F3.wireOp",EDGE,"9f402305-efcd-4aa8-bc8a-3394f6d3dfb0");var subQ1=sQuery(id+"F3.wireOp",EDGE,"E15");var subQ2=makeQuery(id+"F3.imprint","INTERSECT",VERTEX,{"disambiguationData":[OD(0.0)],"derivedFrom":[subQ1,subQ0]});Q43=makeQuery(id+"F3.imprint","IMPRINT",FACE,{"disambiguationData":[TD([[makeQuery(id+"F3.imprint","IMPRINT",EDGE,{"disambiguationData":[TD([[subQ2,-1.0]])],"derivedFrom":subQ1}),-1.0]])]});}
            var Q44;
            {var subQ0=sQuery(id+"F3.wireOp",EDGE,"E38");var subQ1=sQuery(id+"F3.wireOp",EDGE,"E15");var subQ2=makeQuery(id+"F3.imprint","INTERSECT",VERTEX,{"disambiguationData":[OD(0.0)],"derivedFrom":[subQ1,subQ0]});Q44=makeQuery(id+"F3.imprint","IMPRINT",FACE,{"disambiguationData":[TD([[makeQuery(id+"F3.imprint","IMPRINT",EDGE,{"disambiguationData":[TD([[subQ2,-1.0]])],"derivedFrom":subQ1}),1.0]])]});}
            var Q45;
            {var subQ0=sQuery(id+"F3.wireOp",EDGE,"E38");var subQ1=sQuery(id+"F3.wireOp",EDGE,"E15");var subQ2=makeQuery(id+"F3.imprint","INTERSECT",VERTEX,{"disambiguationData":[OD(0.0)],"derivedFrom":[subQ1,subQ0]});Q45=makeQuery(id+"F3.imprint","IMPRINT",FACE,{"disambiguationData":[TD([[makeQuery(id+"F3.imprint","IMPRINT",EDGE,{"disambiguationData":[TD([[subQ2,-1.0]])],"derivedFrom":subQ1}),-1.0]])]});}
            var Q46;
            {var subQ0=sQuery(id+"F3.wireOp",EDGE,"E39");var subQ1=sQuery(id+"F3.wireOp",EDGE,"E15");var subQ2=makeQuery(id+"F3.imprint","INTERSECT",VERTEX,{"disambiguationData":[OD(1.0)],"derivedFrom":[subQ1,subQ0]});Q46=makeQuery(id+"F3.imprint","IMPRINT",FACE,{"disambiguationData":[TD([[makeQuery(id+"F3.imprint","IMPRINT",EDGE,{"disambiguationData":[TD([[subQ2,1.0]])],"derivedFrom":subQ1}),-1.0]])]});}
            var Q47;
            {var subQ0=sQuery(id+"F3.wireOp",EDGE,"E19");var subQ1=sQuery(id+"F3.wireOp",EDGE,"E15");var subQ2=makeQuery(id+"F3.imprint","INTERSECT",VERTEX,{"disambiguationData":[OD(0.0)],"derivedFrom":[subQ1,subQ0]});Q47=makeQuery(id+"F3.imprint","IMPRINT",FACE,{"disambiguationData":[TD([[makeQuery(id+"F3.imprint","IMPRINT",EDGE,{"disambiguationData":[TD([[subQ2,-1.0]])],"derivedFrom":subQ1}),-1.0]])]});}
            var Q48;
            {var subQ0=sQuery(id+"F3.wireOp",EDGE,"E18");var subQ1=sQuery(id+"F3.wireOp",EDGE,"E15");var subQ2=makeQuery(id+"F3.imprint","INTERSECT",VERTEX,{"disambiguationData":[OD(0.0)],"derivedFrom":[subQ1,subQ0]});Q48=makeQuery(id+"F3.imprint","IMPRINT",FACE,{"disambiguationData":[TD([[makeQuery(id+"F3.imprint","IMPRINT",EDGE,{"disambiguationData":[TD([[subQ2,-1.0]])],"derivedFrom":subQ1}),1.0]])]});}
            var Q49;
            {var subQ0=sQuery(id+"F3.wireOp",EDGE,"E17");var subQ1=sQuery(id+"F3.wireOp",EDGE,"E15");var subQ2=makeQuery(id+"F3.imprint","INTERSECT",VERTEX,{"disambiguationData":[OD(0.0)],"derivedFrom":[subQ1,subQ0]});Q49=makeQuery(id+"F3.imprint","IMPRINT",FACE,{"disambiguationData":[TD([[makeQuery(id+"F3.imprint","IMPRINT",EDGE,{"disambiguationData":[TD([[subQ2,-1.0]])],"derivedFrom":subQ1}),1.0]])]});}
            var Q50;
            {var subQ0=sQuery(id+"F3.wireOp",EDGE,"E19");var subQ1=sQuery(id+"F3.wireOp",EDGE,"E15");var subQ2=makeQuery(id+"F3.imprint","INTERSECT",VERTEX,{"disambiguationData":[OD(0.0)],"derivedFrom":[subQ1,subQ0]});Q50=makeQuery(id+"F3.imprint","IMPRINT",FACE,{"disambiguationData":[TD([[makeQuery(id+"F3.imprint","IMPRINT",EDGE,{"disambiguationData":[TD([[subQ2,-1.0]])],"derivedFrom":subQ1}),1.0]])]});}
            var Q51;
            {var subQ0=sQuery(id+"F3.wireOp",EDGE,"E18");var subQ1=sQuery(id+"F3.wireOp",EDGE,"E15");var subQ2=makeQuery(id+"F3.imprint","INTERSECT",VERTEX,{"disambiguationData":[OD(0.0)],"derivedFrom":[subQ1,subQ0]});Q51=makeQuery(id+"F3.imprint","IMPRINT",FACE,{"disambiguationData":[TD([[makeQuery(id+"F3.imprint","IMPRINT",EDGE,{"disambiguationData":[TD([[subQ2,-1.0]])],"derivedFrom":subQ1}),-1.0]])]});}
            var Q52;
            {var subQ0=sQuery(id+"F3.wireOp",EDGE,"E20");var subQ1=sQuery(id+"F3.wireOp",EDGE,"E15");var subQ2=makeQuery(id+"F3.imprint","INTERSECT",VERTEX,{"disambiguationData":[OD(0.0)],"derivedFrom":[subQ1,subQ0]});Q52=makeQuery(id+"F3.imprint","IMPRINT",FACE,{"disambiguationData":[TD([[makeQuery(id+"F3.imprint","IMPRINT",EDGE,{"disambiguationData":[TD([[subQ2,-1.0]])],"derivedFrom":subQ1}),1.0]])]});}
            var Q53;
            {var subQ0=sQuery(id+"F3.wireOp",EDGE,"E17");var subQ1=sQuery(id+"F3.wireOp",EDGE,"E15");var subQ2=makeQuery(id+"F3.imprint","INTERSECT",VERTEX,{"disambiguationData":[OD(0.0)],"derivedFrom":[subQ1,subQ0]});Q53=makeQuery(id+"F3.imprint","IMPRINT",FACE,{"disambiguationData":[TD([[makeQuery(id+"F3.imprint","IMPRINT",EDGE,{"disambiguationData":[TD([[subQ2,-1.0]])],"derivedFrom":subQ1}),-1.0]])]});}
            var Q54;
            {var subQ0=sQuery(id+"F3.wireOp",EDGE,"E20");var subQ1=sQuery(id+"F3.wireOp",EDGE,"E15");var subQ2=makeQuery(id+"F3.imprint","INTERSECT",VERTEX,{"disambiguationData":[OD(0.0)],"derivedFrom":[subQ1,subQ0]});Q54=makeQuery(id+"F3.imprint","IMPRINT",FACE,{"disambiguationData":[TD([[makeQuery(id+"F3.imprint","IMPRINT",EDGE,{"disambiguationData":[TD([[subQ2,-1.0]])],"derivedFrom":subQ1}),-1.0]])]});}
            var Q55;
            Q55=makeQuery(id+"F3.imprint","IMPRINT",FACE,{"disambiguationData":[TD([[makeQuery(id+"F3.imprint","IMPRINT",EDGE,{"derivedFrom":sQuery(id+"F3.wireOp",EDGE,"E16")}),1.0]])]});
            var Q56;
            {var subQ0=sQuery(id+"F3.wireOp",EDGE,"E48");var subQ1=sQuery(id+"F3.wireOp",EDGE,"E15");var subQ2=makeQuery(id+"F3.imprint","INTERSECT",VERTEX,{"disambiguationData":[OD(0.0)],"derivedFrom":[subQ1,subQ0]});Q56=makeQuery(id+"F3.imprint","IMPRINT",FACE,{"disambiguationData":[TD([[makeQuery(id+"F3.imprint","IMPRINT",EDGE,{"disambiguationData":[TD([[subQ2,-1.0]])],"derivedFrom":subQ1}),-1.0]])]});}
            var Q57;
            {var subQ0=sQuery(id+"F3.wireOp",EDGE,"E50");var subQ1=sQuery(id+"F3.wireOp",EDGE,"E15");var subQ2=makeQuery(id+"F3.imprint","INTERSECT",VERTEX,{"disambiguationData":[OD(0.0)],"derivedFrom":[subQ1,subQ0]});Q57=makeQuery(id+"F3.imprint","IMPRINT",FACE,{"disambiguationData":[TD([[makeQuery(id+"F3.imprint","IMPRINT",EDGE,{"disambiguationData":[TD([[subQ2,-1.0]])],"derivedFrom":subQ1}),1.0]])]});}
            var Q58;
            {var subQ0=sQuery(id+"F3.wireOp",EDGE,"E51");var subQ1=sQuery(id+"F3.wireOp",EDGE,"E15");var subQ2=makeQuery(id+"F3.imprint","INTERSECT",VERTEX,{"disambiguationData":[OD(0.0)],"derivedFrom":[subQ1,subQ0]});Q58=makeQuery(id+"F3.imprint","IMPRINT",FACE,{"disambiguationData":[TD([[makeQuery(id+"F3.imprint","IMPRINT",EDGE,{"disambiguationData":[TD([[subQ2,-1.0]])],"derivedFrom":subQ1}),-1.0]])]});}
            var Q59;
            {var subQ0=sQuery(id+"F3.wireOp",EDGE,"E52");var subQ1=sQuery(id+"F3.wireOp",EDGE,"E15");var subQ2=makeQuery(id+"F3.imprint","INTERSECT",VERTEX,{"disambiguationData":[OD(0.0)],"derivedFrom":[subQ1,subQ0]});Q59=makeQuery(id+"F3.imprint","IMPRINT",FACE,{"disambiguationData":[TD([[makeQuery(id+"F3.imprint","IMPRINT",EDGE,{"disambiguationData":[TD([[subQ2,-1.0]])],"derivedFrom":subQ1}),1.0]])]});}
            var Q60;
            {var subQ0=sQuery(id+"F3.wireOp",EDGE,"E49");var subQ1=sQuery(id+"F3.wireOp",EDGE,"E15");var subQ2=makeQuery(id+"F3.imprint","INTERSECT",VERTEX,{"disambiguationData":[OD(0.0)],"derivedFrom":[subQ1,subQ0]});Q60=makeQuery(id+"F3.imprint","IMPRINT",FACE,{"disambiguationData":[TD([[makeQuery(id+"F3.imprint","IMPRINT",EDGE,{"disambiguationData":[TD([[subQ2,-1.0]])],"derivedFrom":subQ1}),-1.0]])]});}
            var Q61;
            {var subQ0=sQuery(id+"F3.wireOp",EDGE,"E48");var subQ1=sQuery(id+"F3.wireOp",EDGE,"E15");var subQ2=makeQuery(id+"F3.imprint","INTERSECT",VERTEX,{"disambiguationData":[OD(0.0)],"derivedFrom":[subQ1,subQ0]});Q61=makeQuery(id+"F3.imprint","IMPRINT",FACE,{"disambiguationData":[TD([[makeQuery(id+"F3.imprint","IMPRINT",EDGE,{"disambiguationData":[TD([[subQ2,-1.0]])],"derivedFrom":subQ1}),1.0]])]});}
            var Q62;
            {var subQ0=sQuery(id+"F3.wireOp",EDGE,"E49");var subQ1=sQuery(id+"F3.wireOp",EDGE,"E15");var subQ2=makeQuery(id+"F3.imprint","INTERSECT",VERTEX,{"disambiguationData":[OD(0.0)],"derivedFrom":[subQ1,subQ0]});Q62=makeQuery(id+"F3.imprint","IMPRINT",FACE,{"disambiguationData":[TD([[makeQuery(id+"F3.imprint","IMPRINT",EDGE,{"disambiguationData":[TD([[subQ2,-1.0]])],"derivedFrom":subQ1}),1.0]])]});}
            var Q63;
            {var subQ0=sQuery(id+"F3.wireOp",EDGE,"E50");var subQ1=sQuery(id+"F3.wireOp",EDGE,"E15");var subQ2=makeQuery(id+"F3.imprint","INTERSECT",VERTEX,{"disambiguationData":[OD(0.0)],"derivedFrom":[subQ1,subQ0]});Q63=makeQuery(id+"F3.imprint","IMPRINT",FACE,{"disambiguationData":[TD([[makeQuery(id+"F3.imprint","IMPRINT",EDGE,{"disambiguationData":[TD([[subQ2,-1.0]])],"derivedFrom":subQ1}),-1.0]])]});}
            var Q64;
            {var subQ0=sQuery(id+"F3.wireOp",EDGE,"E52");var subQ1=sQuery(id+"F3.wireOp",EDGE,"E15");var subQ2=makeQuery(id+"F3.imprint","INTERSECT",VERTEX,{"disambiguationData":[OD(0.0)],"derivedFrom":[subQ1,subQ0]});Q64=makeQuery(id+"F3.imprint","IMPRINT",FACE,{"disambiguationData":[TD([[makeQuery(id+"F3.imprint","IMPRINT",EDGE,{"disambiguationData":[TD([[subQ2,-1.0]])],"derivedFrom":subQ1}),-1.0]])]});}
            var Q65;
            {var subQ0=sQuery(id+"F3.wireOp",EDGE,"E51");var subQ1=sQuery(id+"F3.wireOp",EDGE,"E15");var subQ2=makeQuery(id+"F3.imprint","INTERSECT",VERTEX,{"disambiguationData":[OD(0.0)],"derivedFrom":[subQ1,subQ0]});Q65=makeQuery(id+"F3.imprint","IMPRINT",FACE,{"disambiguationData":[TD([[makeQuery(id+"F3.imprint","IMPRINT",EDGE,{"disambiguationData":[TD([[subQ2,-1.0]])],"derivedFrom":subQ1}),1.0]])]});}
            var Q66;
            {var subQ0=sQuery(id+"F3.wireOp",EDGE,"E43");var subQ1=sQuery(id+"F3.wireOp",EDGE,"E15");var subQ2=makeQuery(id+"F3.imprint","INTERSECT",VERTEX,{"disambiguationData":[OD(0.0)],"derivedFrom":[subQ1,subQ0]});Q66=makeQuery(id+"F3.imprint","IMPRINT",FACE,{"disambiguationData":[TD([[makeQuery(id+"F3.imprint","IMPRINT",EDGE,{"disambiguationData":[TD([[subQ2,-1.0]])],"derivedFrom":subQ1}),-1.0]])]});}
            var Q67;
            {var subQ0=sQuery(id+"F3.wireOp",EDGE,"E47");var subQ1=sQuery(id+"F3.wireOp",EDGE,"E15");var subQ2=makeQuery(id+"F3.imprint","INTERSECT",VERTEX,{"disambiguationData":[OD(0.0)],"derivedFrom":[subQ1,subQ0]});Q67=makeQuery(id+"F3.imprint","IMPRINT",FACE,{"disambiguationData":[TD([[makeQuery(id+"F3.imprint","IMPRINT",EDGE,{"disambiguationData":[TD([[subQ2,-1.0]])],"derivedFrom":subQ1}),1.0]])]});}
            var Q68;
            {var subQ0=sQuery(id+"F3.wireOp",EDGE,"E46");var subQ1=sQuery(id+"F3.wireOp",EDGE,"E15");var subQ2=makeQuery(id+"F3.imprint","INTERSECT",VERTEX,{"disambiguationData":[OD(0.0)],"derivedFrom":[subQ1,subQ0]});Q68=makeQuery(id+"F3.imprint","IMPRINT",FACE,{"disambiguationData":[TD([[makeQuery(id+"F3.imprint","IMPRINT",EDGE,{"disambiguationData":[TD([[subQ2,-1.0]])],"derivedFrom":subQ1}),1.0]])]});}
            var Q69;
            {var subQ0=sQuery(id+"F3.wireOp",EDGE,"E44");var subQ1=sQuery(id+"F3.wireOp",EDGE,"E15");var subQ2=makeQuery(id+"F3.imprint","INTERSECT",VERTEX,{"disambiguationData":[OD(0.0)],"derivedFrom":[subQ1,subQ0]});Q69=makeQuery(id+"F3.imprint","IMPRINT",FACE,{"disambiguationData":[TD([[makeQuery(id+"F3.imprint","IMPRINT",EDGE,{"disambiguationData":[TD([[subQ2,-1.0]])],"derivedFrom":subQ1}),1.0]])]});}
            var Q70;
            {var subQ0=sQuery(id+"F3.wireOp",EDGE,"E45");var subQ1=sQuery(id+"F3.wireOp",EDGE,"E15");var subQ2=makeQuery(id+"F3.imprint","INTERSECT",VERTEX,{"disambiguationData":[OD(0.0)],"derivedFrom":[subQ1,subQ0]});Q70=makeQuery(id+"F3.imprint","IMPRINT",FACE,{"disambiguationData":[TD([[makeQuery(id+"F3.imprint","IMPRINT",EDGE,{"disambiguationData":[TD([[subQ2,-1.0]])],"derivedFrom":subQ1}),-1.0]])]});}
            var Q71;
            {var subQ0=sQuery(id+"F3.wireOp",EDGE,"E46");var subQ1=sQuery(id+"F3.wireOp",EDGE,"E15");var subQ2=makeQuery(id+"F3.imprint","INTERSECT",VERTEX,{"disambiguationData":[OD(0.0)],"derivedFrom":[subQ1,subQ0]});Q71=makeQuery(id+"F3.imprint","IMPRINT",FACE,{"disambiguationData":[TD([[makeQuery(id+"F3.imprint","IMPRINT",EDGE,{"disambiguationData":[TD([[subQ2,-1.0]])],"derivedFrom":subQ1}),-1.0]])]});}
            var Q72;
            {var subQ0=sQuery(id+"F3.wireOp",EDGE,"E47");var subQ1=sQuery(id+"F3.wireOp",EDGE,"E15");var subQ2=makeQuery(id+"F3.imprint","INTERSECT",VERTEX,{"disambiguationData":[OD(0.0)],"derivedFrom":[subQ1,subQ0]});Q72=makeQuery(id+"F3.imprint","IMPRINT",FACE,{"disambiguationData":[TD([[makeQuery(id+"F3.imprint","IMPRINT",EDGE,{"disambiguationData":[TD([[subQ2,-1.0]])],"derivedFrom":subQ1}),-1.0]])]});}
            var Q73;
            {var subQ0=sQuery(id+"F3.wireOp",EDGE,"E45");var subQ1=sQuery(id+"F3.wireOp",EDGE,"E15");var subQ2=makeQuery(id+"F3.imprint","INTERSECT",VERTEX,{"disambiguationData":[OD(0.0)],"derivedFrom":[subQ1,subQ0]});Q73=makeQuery(id+"F3.imprint","IMPRINT",FACE,{"disambiguationData":[TD([[makeQuery(id+"F3.imprint","IMPRINT",EDGE,{"disambiguationData":[TD([[subQ2,-1.0]])],"derivedFrom":subQ1}),1.0]])]});}
            var Q74;
            {var subQ0=sQuery(id+"F3.wireOp",EDGE,"E44");var subQ1=sQuery(id+"F3.wireOp",EDGE,"E15");var subQ2=makeQuery(id+"F3.imprint","INTERSECT",VERTEX,{"disambiguationData":[OD(0.0)],"derivedFrom":[subQ1,subQ0]});Q74=makeQuery(id+"F3.imprint","IMPRINT",FACE,{"disambiguationData":[TD([[makeQuery(id+"F3.imprint","IMPRINT",EDGE,{"disambiguationData":[TD([[subQ2,-1.0]])],"derivedFrom":subQ1}),-1.0]])]});}
            var Q75;
            {var subQ0=sQuery(id+"F3.wireOp",EDGE,"E43");var subQ1=sQuery(id+"F3.wireOp",EDGE,"E15");var subQ2=makeQuery(id+"F3.imprint","INTERSECT",VERTEX,{"disambiguationData":[OD(0.0)],"derivedFrom":[subQ1,subQ0]});Q75=makeQuery(id+"F3.imprint","IMPRINT",FACE,{"disambiguationData":[TD([[makeQuery(id+"F3.imprint","IMPRINT",EDGE,{"disambiguationData":[TD([[subQ2,-1.0]])],"derivedFrom":subQ1}),1.0]])]});}
            var Q76;
            {var subQ0=sQuery(id+"F3.wireOp",EDGE,"E57");var subQ1=sQuery(id+"F3.wireOp",EDGE,"E15");var subQ2=makeQuery(id+"F3.imprint","INTERSECT",VERTEX,{"disambiguationData":[OD(0.0)],"derivedFrom":[subQ1,subQ0]});Q76=makeQuery(id+"F3.imprint","IMPRINT",FACE,{"disambiguationData":[TD([[makeQuery(id+"F3.imprint","IMPRINT",EDGE,{"disambiguationData":[TD([[subQ2,-1.0]])],"derivedFrom":subQ1}),1.0]])]});}
            var Q77;
            {var subQ0=sQuery(id+"F3.wireOp",EDGE,"E54");var subQ1=sQuery(id+"F3.wireOp",EDGE,"E15");var subQ2=makeQuery(id+"F3.imprint","INTERSECT",VERTEX,{"disambiguationData":[OD(0.0)],"derivedFrom":[subQ1,subQ0]});Q77=makeQuery(id+"F3.imprint","IMPRINT",FACE,{"disambiguationData":[TD([[makeQuery(id+"F3.imprint","IMPRINT",EDGE,{"disambiguationData":[TD([[subQ2,-1.0]])],"derivedFrom":subQ1}),1.0]])]});}
            var Q78;
            {var subQ0=sQuery(id+"F3.wireOp",EDGE,"E53");var subQ1=sQuery(id+"F3.wireOp",EDGE,"E15");var subQ2=makeQuery(id+"F3.imprint","INTERSECT",VERTEX,{"disambiguationData":[OD(0.0)],"derivedFrom":[subQ1,subQ0]});Q78=makeQuery(id+"F3.imprint","IMPRINT",FACE,{"disambiguationData":[TD([[makeQuery(id+"F3.imprint","IMPRINT",EDGE,{"disambiguationData":[TD([[subQ2,-1.0]])],"derivedFrom":subQ1}),-1.0]])]});}
            var Q79;
            {var subQ0=sQuery(id+"F3.wireOp",EDGE,"E56");var subQ1=sQuery(id+"F3.wireOp",EDGE,"E15");var subQ2=makeQuery(id+"F3.imprint","INTERSECT",VERTEX,{"disambiguationData":[OD(0.0)],"derivedFrom":[subQ1,subQ0]});Q79=makeQuery(id+"F3.imprint","IMPRINT",FACE,{"disambiguationData":[TD([[makeQuery(id+"F3.imprint","IMPRINT",EDGE,{"disambiguationData":[TD([[subQ2,-1.0]])],"derivedFrom":subQ1}),-1.0]])]});}
            var Q80;
            {var subQ0=sQuery(id+"F3.wireOp",EDGE,"E53");var subQ1=sQuery(id+"F3.wireOp",EDGE,"E15");var subQ2=makeQuery(id+"F3.imprint","INTERSECT",VERTEX,{"disambiguationData":[OD(0.0)],"derivedFrom":[subQ1,subQ0]});Q80=makeQuery(id+"F3.imprint","IMPRINT",FACE,{"disambiguationData":[TD([[makeQuery(id+"F3.imprint","IMPRINT",EDGE,{"disambiguationData":[TD([[subQ2,-1.0]])],"derivedFrom":subQ1}),1.0]])]});}
            var Q81;
            {var subQ0=sQuery(id+"F3.wireOp",EDGE,"E56");var subQ1=sQuery(id+"F3.wireOp",EDGE,"E15");var subQ2=makeQuery(id+"F3.imprint","INTERSECT",VERTEX,{"disambiguationData":[OD(0.0)],"derivedFrom":[subQ1,subQ0]});Q81=makeQuery(id+"F3.imprint","IMPRINT",FACE,{"disambiguationData":[TD([[makeQuery(id+"F3.imprint","IMPRINT",EDGE,{"disambiguationData":[TD([[subQ2,-1.0]])],"derivedFrom":subQ1}),1.0]])]});}
            var Q82;
            {var subQ0=sQuery(id+"F3.wireOp",EDGE,"E57");var subQ1=sQuery(id+"F3.wireOp",EDGE,"E15");var subQ2=makeQuery(id+"F3.imprint","INTERSECT",VERTEX,{"disambiguationData":[OD(0.0)],"derivedFrom":[subQ1,subQ0]});Q82=makeQuery(id+"F3.imprint","IMPRINT",FACE,{"disambiguationData":[TD([[makeQuery(id+"F3.imprint","IMPRINT",EDGE,{"disambiguationData":[TD([[subQ2,-1.0]])],"derivedFrom":subQ1}),-1.0]])]});}
            var Q83;
            {var subQ0=sQuery(id+"F3.wireOp",EDGE,"E55");var subQ1=sQuery(id+"F3.wireOp",EDGE,"E15");var subQ2=makeQuery(id+"F3.imprint","INTERSECT",VERTEX,{"disambiguationData":[OD(0.0)],"derivedFrom":[subQ1,subQ0]});Q83=makeQuery(id+"F3.imprint","IMPRINT",FACE,{"disambiguationData":[TD([[makeQuery(id+"F3.imprint","IMPRINT",EDGE,{"disambiguationData":[TD([[subQ2,-1.0]])],"derivedFrom":subQ1}),-1.0]])]});}
            var Q84;
            {var subQ0=sQuery(id+"F3.wireOp",EDGE,"E55");var subQ1=sQuery(id+"F3.wireOp",EDGE,"E15");var subQ2=makeQuery(id+"F3.imprint","INTERSECT",VERTEX,{"disambiguationData":[OD(0.0)],"derivedFrom":[subQ1,subQ0]});Q84=makeQuery(id+"F3.imprint","IMPRINT",FACE,{"disambiguationData":[TD([[makeQuery(id+"F3.imprint","IMPRINT",EDGE,{"disambiguationData":[TD([[subQ2,-1.0]])],"derivedFrom":subQ1}),1.0]])]});}
            var Q85;
            {var subQ0=sQuery(id+"F3.wireOp",EDGE,"E54");var subQ1=sQuery(id+"F3.wireOp",EDGE,"E15");var subQ2=makeQuery(id+"F3.imprint","INTERSECT",VERTEX,{"disambiguationData":[OD(0.0)],"derivedFrom":[subQ1,subQ0]});Q85=makeQuery(id+"F3.imprint","IMPRINT",FACE,{"disambiguationData":[TD([[makeQuery(id+"F3.imprint","IMPRINT",EDGE,{"disambiguationData":[TD([[subQ2,-1.0]])],"derivedFrom":subQ1}),-1.0]])]});}
            var Q86;
            Q86=sQuery(id+"F3.wireOp",EDGE,"E19");
            var Q87;
            Q87=sQuery(id+"F3.wireOp",EDGE,"E53");
            var Q88;
            Q88=sQuery(id+"F3.wireOp",EDGE,"E17");
            var Q89;
            Q89=sQuery(id+"F3.wireOp",EDGE,"E18");
            var Q90;
            Q90=sQuery(id+"F3.wireOp",EDGE,"E54");
            var Q91;
            Q91=sQuery(id+"F3.wireOp",EDGE,"E56");
            var Q92;
            Q92=sQuery(id+"F3.wireOp",EDGE,"E55");
            var Q93;
            Q93=sQuery(id+"F3.wireOp",EDGE,"E51");
            var Q94;
            Q94=sQuery(id+"F3.wireOp",EDGE,"E48");
            var Q95;
            Q95=sQuery(id+"F3.wireOp",EDGE,"E41");
            var Q96;
            Q96=sQuery(id+"F3.wireOp",EDGE,"E33");
            var Q97;
            Q97=sQuery(id+"F3.wireOp",EDGE,"E42");
            var Q98;
            Q98=sQuery(id+"F3.wireOp",EDGE,"E30");
            var Q99;
            Q99=sQuery(id+"F3.wireOp",EDGE,"E46");
            var Q100;
            Q100=sQuery(id+"F3.wireOp",EDGE,"E37");
            var Q101;
            Q101=sQuery(id+"F3.wireOp",EDGE,"E22");
            var Q102;
            Q102=sQuery(id+"F3.wireOp",EDGE,"E20");
            var Q103;
            Q103=sQuery(id+"F3.wireOp",EDGE,"E50");
            var Q104;
            Q104=sQuery(id+"F3.wireOp",EDGE,"E31");
            var Q105;
            Q105=sQuery(id+"F3.wireOp",EDGE,"E27");
            var Q106;
            Q106=sQuery(id+"F3.wireOp",EDGE,"E28");
            var Q107;
            Q107=sQuery(id+"F3.wireOp",EDGE,"E49");
            var Q108;
            Q108=sQuery(id+"F3.wireOp",EDGE,"E43");
            var Q109;
            Q109=sQuery(id+"F3.wireOp",EDGE,"E34");
            var Q110;
            Q110=sQuery(id+"F3.wireOp",EDGE,"E36");
            var Q111;
            Q111=sQuery(id+"F3.wireOp",EDGE,"E52");
            var Q112;
            Q112=sQuery(id+"F3.wireOp",EDGE,"E35");
            var Q113;
            Q113=sQuery(id+"F3.wireOp",EDGE,"E24");
            var Q114;
            Q114=sQuery(id+"F3.wireOp",EDGE,"E21");
            var Q115;
            Q115=sQuery(id+"F3.wireOp",EDGE,"E26");
            var Q116;
            Q116=sQuery(id+"F3.wireOp",EDGE,"E29");
            var Q117;
            Q117=sQuery(id+"F3.wireOp",EDGE,"E44");
            var Q118;
            Q118=sQuery(id+"F3.wireOp",EDGE,"E45");
            var Q119;
            Q119=sQuery(id+"F3.wireOp",EDGE,"E39");
            var Q120;
            Q120=sQuery(id+"F3.wireOp",EDGE,"E23");
            var Q121;
            Q121=sQuery(id+"F3.wireOp",EDGE,"9f402305-efcd-4aa8-bc8a-3394f6d3dfb0");
            var Q122;
            Q122=sQuery(id+"F3.wireOp",EDGE,"E40");
            var Q123;
            Q123=sQuery(id+"F3.wireOp",EDGE,"E47");
            var Q124;
            Q124=sQuery(id+"F3.wireOp",EDGE,"E25");
            var Q125;
            Q125=sQuery(id+"F3.wireOp",EDGE,"E32");
            var Q126;
            Q126=sQuery(id+"F3.wireOp",EDGE,"E38");
            var Q127;
            Q127=sQuery(id+"F3.wireOp",EDGE,"E16");
            var Q128;
            Q128=sQuery(id+"F3.wireOp",EDGE,"E57");
            extrude(context, id + "F6", {"entities" : qUnion([Q0, Q1, Q2, Q3, Q4, Q5, Q6, Q7, Q8, Q9, Q10, Q11, Q12, Q13, Q14, Q15, Q16, Q17, Q18, Q19, Q20, Q21, Q22, Q23, Q24, Q25, Q26, Q27, Q28, Q29, Q30, Q31, Q32, Q33, Q34, Q35, Q36, Q37, Q38, Q39, Q40, Q41, Q42, Q43, Q44, Q45, Q46, Q47, Q48, Q49, Q50, Q51, Q52, Q53, Q54, Q55, Q56, Q57, Q58, Q59, Q60, Q61, Q62, Q63, Q64, Q65, Q66, Q67, Q68, Q69, Q70, Q71, Q72, Q73, Q74, Q75, Q76, Q77, Q78, Q79, Q80, Q81, Q82, Q83, Q84, Q85]), "surfaceEntities" : qUnion([Q86, Q87, Q88, Q89, Q90, Q91, Q92, Q93, Q94, Q95, Q96, Q97, Q98, Q99, Q100, Q101, Q102, Q103, Q104, Q105, Q106, Q107, Q108, Q109, Q110, Q111, Q112, Q113, Q114, Q115, Q116, Q117, Q118, Q119, Q120, Q121, Q122, Q123, Q124, Q125, Q126, Q127, Q128]), "depth" : 508 * mm});
        }
    });
